# Revit family: WHCHS
name_source: partatom
category: Mechanical Equipment
revit_build: Autodesk Revit MEP 2016 (Build: 20150220_1215(x64)
units: mm (PartAtom-declared; Revit-internal decimal feet)

## family parameters
Cut with Voids When Loaded = No
Host = Face
OmniClass Number = 23.45.05.14.17
OmniClass Title = Showers
Part Type = Normal
Room Calculation Point = No
Round Connector Dimension = Use Diameter
Shared = Yes

## types (4) — shared parameters
Tempered Water Connection = Yes
Vent Connection = No
Waste Connection = No
zero-valued in all types: Amperage, Voltage

## per-type parameters (varying)
| type | Assembly Code | CW Connection | Default Elevation | Description | HW Connection | Manufacturer | Material | Model | OVERALL DEPTH | OVERALL SIZE HEIGHT | OVERALL SIZE WIDTH | Revised Date | URL |
| WHCHS |  | No | 60 " | Ligature Resistant Handheld Shower and Collapsible Handheld Shower Mounting Bracket | No | Whitehall Manufacturing | Stainless Steel | WHCHS | 1 | 5 | 5 | 03/03/2020 | https://www.whitehallmfg.com |
| 1146-002-001-CSH | D2010710 | Yes | 72 " | Conical Showerhead (Ligature Resistant) | Yes | Acorn Engineering Company | Stainless Steel-Acorn-Type 304-Satin | CSH | 2.5 | 2 | 2.5 | 09/21/2015 | http://www.acorneng.com |
| RD-SOAP DISH | D2010710 | Yes | 72 " | Acorn Shower-Ware® 410B Series Apex Type 1 Flush-Mounted Shower | Yes | Acorn Engineering Company | Stainless Steel-Acorn-Type 304-Satin | 418B-W-RD | 2.5 | 2 | 2.5 | 09/21/2015 | http://www.acorneng.com |
| 7000-012-000 bubbler |  | No | 0 " | -CSH- Conical ShowerHead | No | Acorn Engineering Co | Stainless Steel | 1176-002-001 | 2.5 | 2 | 2.5 | 09/21/2015 | http://www.murdockmfg.com |

## geometry (parser evidence)
native form markers: Sweep x1
no freeform markers — native parametric forms only
